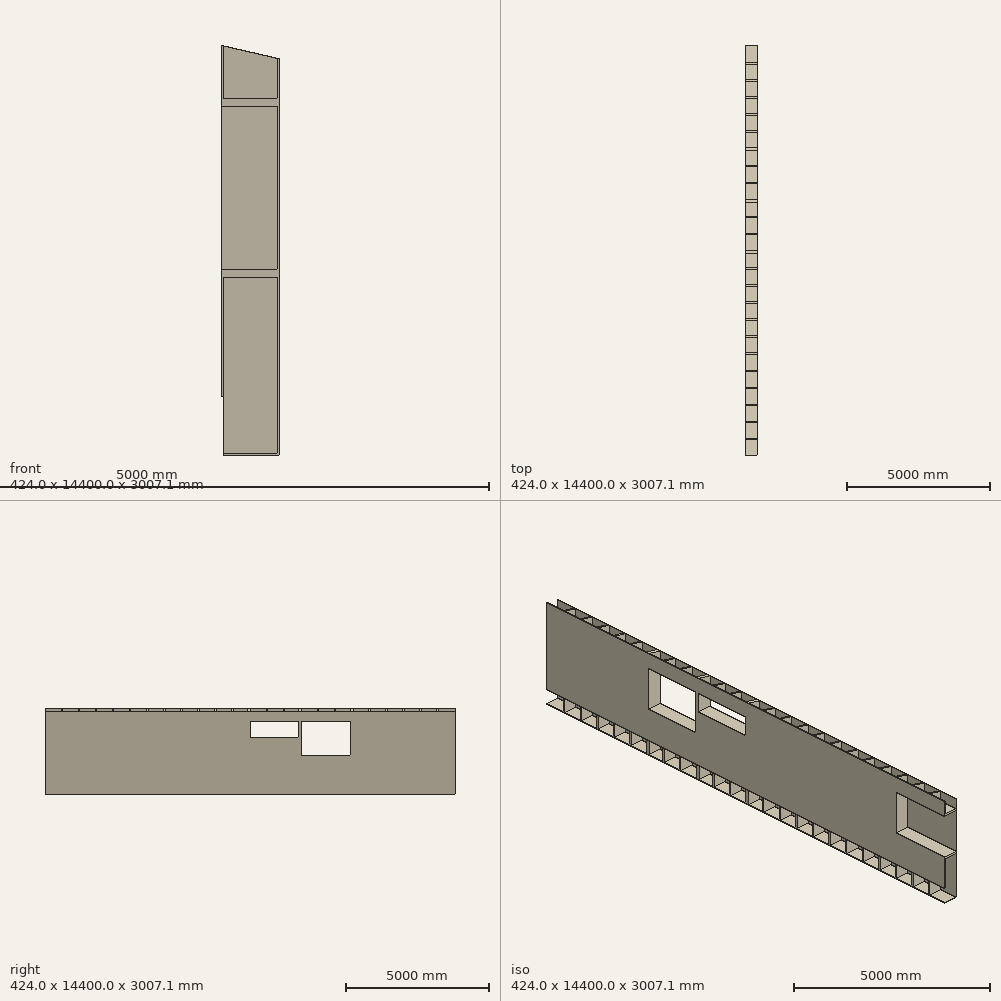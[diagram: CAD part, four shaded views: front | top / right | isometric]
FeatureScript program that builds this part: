
annotation { "Feature Type Name" : "Feature", "Feature Type Description" : "" }
export const myFeature = defineFeature(function(context is Context, id is Id, definition is map)
    precondition{}
    {
        {
            var Q0;
            Q0=qCreatedBy(makeId("Right.planeOp"),FACE);
            var sketch = newSketch(context, id + "F0", { "sketchPlane" : qUnion([Q0])});
            skLineSegment(sketch, "E0.bottom", {"start": v(0, 0) * mm, "end": v(14400, 0) * mm});
            skLineSegment(sketch, "E0.top", {"start": v(0, 3200) * mm, "end": v(14400, 3200) * mm});
            skLineSegment(sketch, "E0.left", {"start": v(0, 0) * mm, "end": v(0, 3200) * mm});
            skLineSegment(sketch, "E0.right", {"start": v(14400, 0) * mm, "end": v(14400, 3200) * mm});
            skLineSegment(sketch, "E1", {"start": v(549, 3200) * mm, "end": v(549, 2610) * mm});
            skLineSegment(sketch, "E2", {"start": v(600, 3200) * mm, "end": v(600, 2610) * mm});
            skLineSegment(sketch, "E3.1.0.0", {"start": v(1149, 3200) * mm, "end": v(1149, 2610) * mm});
            skLineSegment(sketch, "E3.1.0.1", {"start": v(1200, 3200) * mm, "end": v(1200, 2610) * mm});
            skLineSegment(sketch, "E3.2.0.0", {"start": v(1749, 3200) * mm, "end": v(1749, 0) * mm});
            skLineSegment(sketch, "E3.2.0.1", {"start": v(1800, 3200) * mm, "end": v(1800, 0) * mm});
            skLineSegment(sketch, "E3.3.0.0", {"start": v(2349, 3200) * mm, "end": v(2349, 0) * mm});
            skLineSegment(sketch, "E3.3.0.1", {"start": v(2400, 3200) * mm, "end": v(2400, 0) * mm});
            skLineSegment(sketch, "E3.4.0.0", {"start": v(2949, 3200) * mm, "end": v(2949, 0) * mm});
            skLineSegment(sketch, "E3.4.0.1", {"start": v(3000, 3200) * mm, "end": v(3000, 0) * mm});
            skLineSegment(sketch, "E3.5.0.0", {"start": v(3549, 3200) * mm, "end": v(3549, 0) * mm});
            skLineSegment(sketch, "E3.5.0.1", {"start": v(3600, 3200) * mm, "end": v(3600, 0) * mm});
            skLineSegment(sketch, "E3.6.0.0", {"start": v(4149, 3200) * mm, "end": v(4149, 0) * mm});
            skLineSegment(sketch, "E3.6.0.1", {"start": v(4200, 3200) * mm, "end": v(4200, 0) * mm});
            skLineSegment(sketch, "E3.7.0.0", {"start": v(4749, 3200) * mm, "end": v(4749, 0) * mm});
            skLineSegment(sketch, "E3.7.0.1", {"start": v(4800, 3200) * mm, "end": v(4800, 0) * mm});
            skLineSegment(sketch, "E3.8.0.0", {"start": v(5349, 3200) * mm, "end": v(5349, 0) * mm});
            skLineSegment(sketch, "E3.8.0.1", {"start": v(5400, 3200) * mm, "end": v(5400, 0) * mm});
            skLineSegment(sketch, "E3.9.0.0", {"start": v(5949, 3200) * mm, "end": v(5949, 0) * mm});
            skLineSegment(sketch, "E3.9.0.1", {"start": v(6000, 3200) * mm, "end": v(6000, 0) * mm});
            skLineSegment(sketch, "E3.10.0.0", {"start": v(6549, 3200) * mm, "end": v(6549, 0) * mm});
            skLineSegment(sketch, "E3.10.0.1", {"start": v(6600, 3200) * mm, "end": v(6600, 0) * mm});
            skLineSegment(sketch, "E3.11.0.1", {"start": v(7200, 3200) * mm, "end": v(7200, 2000) * mm});
            skLineSegment(sketch, "E3.12.0.0", {"start": v(7749, 3200) * mm, "end": v(7749, 2610) * mm});
            skLineSegment(sketch, "E3.12.0.1", {"start": v(7800, 3200) * mm, "end": v(7800, 2610) * mm});
            skLineSegment(sketch, "E3.13.0.0", {"start": v(8349, 3200) * mm, "end": v(8349, 2610) * mm});
            skLineSegment(sketch, "E3.13.0.1", {"start": v(8400, 3200) * mm, "end": v(8400, 2610) * mm});
            skLineSegment(sketch, "E3.14.0.1", {"start": v(9000, 3200) * mm, "end": v(9000, 2610) * mm});
            skLineSegment(sketch, "E3.15.0.0", {"start": v(9549, 3200) * mm, "end": v(9549, 2610) * mm});
            skLineSegment(sketch, "E3.15.0.1", {"start": v(9600, 3200) * mm, "end": v(9600, 2610) * mm});
            skLineSegment(sketch, "E3.16.0.0", {"start": v(10149, 3200) * mm, "end": v(10149, 2610) * mm});
            skLineSegment(sketch, "E3.16.0.1", {"start": v(10200, 3200) * mm, "end": v(10200, 2610) * mm});
            skLineSegment(sketch, "E3.17.0.0", {"start": v(10749, 3200) * mm, "end": v(10749, 0) * mm});
            skLineSegment(sketch, "E3.17.0.1", {"start": v(10800, 3200) * mm, "end": v(10800, 0) * mm});
            skLineSegment(sketch, "E3.18.0.0", {"start": v(11349, 3200) * mm, "end": v(11349, 0) * mm});
            skLineSegment(sketch, "E3.18.0.1", {"start": v(11400, 3200) * mm, "end": v(11400, 0) * mm});
            skLineSegment(sketch, "E3.19.0.0", {"start": v(11949, 3200) * mm, "end": v(11949, 0) * mm});
            skLineSegment(sketch, "E3.19.0.1", {"start": v(12000, 3200) * mm, "end": v(12000, 0) * mm});
            skLineSegment(sketch, "E3.20.0.0", {"start": v(12549, 3200) * mm, "end": v(12549, 0) * mm});
            skLineSegment(sketch, "E3.20.0.1", {"start": v(12600, 3200) * mm, "end": v(12600, 0) * mm});
            skLineSegment(sketch, "E3.21.0.0", {"start": v(13149, 3200) * mm, "end": v(13149, 0) * mm});
            skLineSegment(sketch, "E3.21.0.1", {"start": v(13200, 3200) * mm, "end": v(13200, 0) * mm});
            skLineSegment(sketch, "E3.22.0.0", {"start": v(13749, 3200) * mm, "end": v(13749, 0) * mm});
            skLineSegment(sketch, "E3.22.0.1", {"start": v(13800, 3200) * mm, "end": v(13800, 0) * mm});
            skLineSegment(sketch, "E3.direction1", {"start": v(549, 0) * mm, "end": v(1149, 0) * mm, "construction": true});
            skLineSegment(sketch, "E4", {"start": v(0, 2550) * mm, "end": v(1749, 2550) * mm});
            skLineSegment(sketch, "E5", {"start": v(0, 2610) * mm, "end": v(1749, 2610) * mm});
            skLineSegment(sketch, "E6", {"start": v(1740, 2550) * mm, "end": v(1740, 1350) * mm});
            skLineSegment(sketch, "E7", {"start": v(1749, 1350) * mm, "end": v(0, 1350) * mm});
            skLineSegment(sketch, "E8", {"start": v(1749, 1290) * mm, "end": v(0, 1290) * mm});
            skLineSegment(sketch, "E9.trimOffspring", {"start": v(549, 1290) * mm, "end": v(549, 0) * mm});
            skLineSegment(sketch, "E10.trimOffspring", {"start": v(600, 1290) * mm, "end": v(600, 0) * mm});
            skLineSegment(sketch, "E11.trimOffspring", {"start": v(1149, 1290) * mm, "end": v(1149, 0) * mm});
            skLineSegment(sketch, "E12.trimOffspring", {"start": v(1200, 1290) * mm, "end": v(1200, 0) * mm});
            skLineSegment(sketch, "E13", {"start": v(7200, 2610) * mm, "end": v(8898, 2610) * mm});
            skLineSegment(sketch, "E14", {"start": v(7200, 2550) * mm, "end": v(8898, 2550) * mm});
            skLineSegment(sketch, "E15", {"start": v(7200, 2000) * mm, "end": v(8898, 2000) * mm});
            skLineSegment(sketch, "E16", {"start": v(7200, 1940) * mm, "end": v(8898, 1940) * mm});
            skLineSegment(sketch, "E17.trimOffspring", {"start": v(7149, 3200) * mm, "end": v(7149, 0) * mm});
            skLineSegment(sketch, "E18.trimOffspring", {"start": v(7200, 1940) * mm, "end": v(7200, 0) * mm});
            skLineSegment(sketch, "E19.trimOffspring", {"start": v(7749, 1940) * mm, "end": v(7749, 0) * mm});
            skLineSegment(sketch, "E20.trimOffspring", {"start": v(7800, 1940) * mm, "end": v(7800, 0) * mm});
            skLineSegment(sketch, "E21", {"start": v(7098, 3200) * mm, "end": v(7098, 0) * mm});
            skLineSegment(sketch, "E22", {"start": v(9000, 3200) * mm, "end": v(9000, 0) * mm});
            skLineSegment(sketch, "E23", {"start": v(9000, 2610) * mm, "end": v(10698, 2610) * mm});
            skLineSegment(sketch, "E24", {"start": v(9000, 2550) * mm, "end": v(10698, 2550) * mm});
            skLineSegment(sketch, "E25", {"start": v(9000, 1350) * mm, "end": v(10698, 1350) * mm});
            skLineSegment(sketch, "E26", {"start": v(9000, 1290) * mm, "end": v(10698, 1290) * mm});
            skLineSegment(sketch, "E27.trimOffspring", {"start": v(8949, 3200) * mm, "end": v(8949, 0) * mm});
            skLineSegment(sketch, "E28.trimOffspring", {"start": v(9000, 1290) * mm, "end": v(9000, 0) * mm});
            skLineSegment(sketch, "E29.trimOffspring", {"start": v(9549, 1290) * mm, "end": v(9549, 0) * mm});
            skLineSegment(sketch, "E30.trimOffspring", {"start": v(9600, 1290) * mm, "end": v(9600, 0) * mm});
            skLineSegment(sketch, "E31.trimOffspring", {"start": v(10149, 1290) * mm, "end": v(10149, 0) * mm});
            skLineSegment(sketch, "E32.trimOffspring", {"start": v(8349, 1940) * mm, "end": v(8349, 0) * mm});
            skLineSegment(sketch, "E33.trimOffspring", {"start": v(8400, 1940) * mm, "end": v(8400, 0) * mm});
            skLineSegment(sketch, "E34", {"start": v(8898, 3200) * mm, "end": v(8898, 0) * mm});
            skLineSegment(sketch, "E35.trimOffspring", {"start": v(10200, 1290) * mm, "end": v(10200, 0) * mm});
            skLineSegment(sketch, "E36", {"start": v(10698, 3200) * mm, "end": v(10698, 0) * mm});
            skSolve(sketch);
        }
        {
            var Q0;
            {var subQ0=sQuery(id+"F0.wireOp",EDGE,"E1");Q0=makeQuery(id+"F0.imprint","IMPRINT",FACE,{"disambiguationData":[TD([[makeQuery(id+"F0.imprint","IMPRINT",EDGE,{"derivedFrom":subQ0}),1.0]])]});}
            var Q1;
            {var subQ0=sQuery(id+"F0.wireOp",EDGE,"E3.1.0.0");Q1=makeQuery(id+"F0.imprint","IMPRINT",FACE,{"disambiguationData":[TD([[makeQuery(id+"F0.imprint","IMPRINT",EDGE,{"derivedFrom":subQ0}),1.0]])]});}
            var Q2;
            {var subQ0=sQuery(id+"F0.wireOp",EDGE,"E3.2.0.0");Q2=makeQuery(id+"F0.imprint","IMPRINT",FACE,{"disambiguationData":[TD([[makeQuery(id+"F0.imprint","IMPRINT",EDGE,{"derivedFrom":subQ0}),1.0]])]});}
            var Q3;
            {var subQ0=sQuery(id+"F0.wireOp",EDGE,"E3.3.0.0");Q3=makeQuery(id+"F0.imprint","IMPRINT",FACE,{"disambiguationData":[TD([[makeQuery(id+"F0.imprint","IMPRINT",EDGE,{"derivedFrom":subQ0}),1.0]])]});}
            var Q4;
            {var subQ0=sQuery(id+"F0.wireOp",EDGE,"E3.4.0.0");Q4=makeQuery(id+"F0.imprint","IMPRINT",FACE,{"disambiguationData":[TD([[makeQuery(id+"F0.imprint","IMPRINT",EDGE,{"derivedFrom":subQ0}),1.0]])]});}
            var Q5;
            {var subQ0=sQuery(id+"F0.wireOp",EDGE,"E3.5.0.0");Q5=makeQuery(id+"F0.imprint","IMPRINT",FACE,{"disambiguationData":[TD([[makeQuery(id+"F0.imprint","IMPRINT",EDGE,{"derivedFrom":subQ0}),1.0]])]});}
            var Q6;
            {var subQ0=sQuery(id+"F0.wireOp",EDGE,"E3.6.0.0");Q6=makeQuery(id+"F0.imprint","IMPRINT",FACE,{"disambiguationData":[TD([[makeQuery(id+"F0.imprint","IMPRINT",EDGE,{"derivedFrom":subQ0}),1.0]])]});}
            var Q7;
            {var subQ0=sQuery(id+"F0.wireOp",EDGE,"E3.7.0.0");Q7=makeQuery(id+"F0.imprint","IMPRINT",FACE,{"disambiguationData":[TD([[makeQuery(id+"F0.imprint","IMPRINT",EDGE,{"derivedFrom":subQ0}),1.0]])]});}
            var Q8;
            {var subQ0=sQuery(id+"F0.wireOp",EDGE,"E3.8.0.0");Q8=makeQuery(id+"F0.imprint","IMPRINT",FACE,{"disambiguationData":[TD([[makeQuery(id+"F0.imprint","IMPRINT",EDGE,{"derivedFrom":subQ0}),1.0]])]});}
            var Q9;
            {var subQ0=sQuery(id+"F0.wireOp",EDGE,"E3.9.0.0");Q9=makeQuery(id+"F0.imprint","IMPRINT",FACE,{"disambiguationData":[TD([[makeQuery(id+"F0.imprint","IMPRINT",EDGE,{"derivedFrom":subQ0}),1.0]])]});}
            var Q10;
            {var subQ0=sQuery(id+"F0.wireOp",EDGE,"E3.10.0.0");Q10=makeQuery(id+"F0.imprint","IMPRINT",FACE,{"disambiguationData":[TD([[makeQuery(id+"F0.imprint","IMPRINT",EDGE,{"derivedFrom":subQ0}),1.0]])]});}
            var Q11;
            {var subQ0=sQuery(id+"F0.wireOp",EDGE,"E3.11.0.0");Q11=makeQuery(id+"F0.imprint","IMPRINT",FACE,{"disambiguationData":[TD([[makeQuery(id+"F0.imprint","IMPRINT",EDGE,{"derivedFrom":subQ0}),1.0]])]});}
            var Q12;
            {var subQ0=sQuery(id+"F0.wireOp",EDGE,"E3.12.0.0");Q12=makeQuery(id+"F0.imprint","IMPRINT",FACE,{"disambiguationData":[TD([[makeQuery(id+"F0.imprint","IMPRINT",EDGE,{"derivedFrom":subQ0}),1.0]])]});}
            var Q13;
            {var subQ0=sQuery(id+"F0.wireOp",EDGE,"E3.13.0.0");Q13=makeQuery(id+"F0.imprint","IMPRINT",FACE,{"disambiguationData":[TD([[makeQuery(id+"F0.imprint","IMPRINT",EDGE,{"derivedFrom":subQ0}),1.0]])]});}
            var Q14;
            {var subQ0=sQuery(id+"F0.wireOp",EDGE,"E3.14.0.0");Q14=makeQuery(id+"F0.imprint","IMPRINT",FACE,{"disambiguationData":[TD([[makeQuery(id+"F0.imprint","IMPRINT",EDGE,{"derivedFrom":subQ0}),1.0]])]});}
            var Q15;
            {var subQ0=sQuery(id+"F0.wireOp",EDGE,"E3.15.0.0");Q15=makeQuery(id+"F0.imprint","IMPRINT",FACE,{"disambiguationData":[TD([[makeQuery(id+"F0.imprint","IMPRINT",EDGE,{"derivedFrom":subQ0}),1.0]])]});}
            var Q16;
            {var subQ0=sQuery(id+"F0.wireOp",EDGE,"E3.16.0.0");Q16=makeQuery(id+"F0.imprint","IMPRINT",FACE,{"disambiguationData":[TD([[makeQuery(id+"F0.imprint","IMPRINT",EDGE,{"derivedFrom":subQ0}),1.0]])]});}
            var Q17;
            {var subQ0=sQuery(id+"F0.wireOp",EDGE,"E3.17.0.0");Q17=makeQuery(id+"F0.imprint","IMPRINT",FACE,{"disambiguationData":[TD([[makeQuery(id+"F0.imprint","IMPRINT",EDGE,{"derivedFrom":subQ0}),1.0]])]});}
            var Q18;
            {var subQ0=sQuery(id+"F0.wireOp",EDGE,"E3.18.0.0");Q18=makeQuery(id+"F0.imprint","IMPRINT",FACE,{"disambiguationData":[TD([[makeQuery(id+"F0.imprint","IMPRINT",EDGE,{"derivedFrom":subQ0}),1.0]])]});}
            var Q19;
            {var subQ0=sQuery(id+"F0.wireOp",EDGE,"E3.19.0.0");Q19=makeQuery(id+"F0.imprint","IMPRINT",FACE,{"disambiguationData":[TD([[makeQuery(id+"F0.imprint","IMPRINT",EDGE,{"derivedFrom":subQ0}),1.0]])]});}
            var Q20;
            {var subQ0=sQuery(id+"F0.wireOp",EDGE,"E3.20.0.0");Q20=makeQuery(id+"F0.imprint","IMPRINT",FACE,{"disambiguationData":[TD([[makeQuery(id+"F0.imprint","IMPRINT",EDGE,{"derivedFrom":subQ0}),1.0]])]});}
            var Q21;
            {var subQ0=sQuery(id+"F0.wireOp",EDGE,"E3.21.0.0");Q21=makeQuery(id+"F0.imprint","IMPRINT",FACE,{"disambiguationData":[TD([[makeQuery(id+"F0.imprint","IMPRINT",EDGE,{"derivedFrom":subQ0}),1.0]])]});}
            var Q22;
            {var subQ0=sQuery(id+"F0.wireOp",EDGE,"E3.22.0.0");Q22=makeQuery(id+"F0.imprint","IMPRINT",FACE,{"disambiguationData":[TD([[makeQuery(id+"F0.imprint","IMPRINT",EDGE,{"derivedFrom":subQ0}),1.0]])]});}
            var Q23;
            {var subQ0=sQuery(id+"F0.wireOp",EDGE,"E4");var subQ4=sQuery(id+"F0.wireOp",EDGE,"E0.left");var subQ5=makeQuery(id+"F0.imprint","INTERSECT",VERTEX,{"derivedFrom":[subQ4,subQ0]});Q23=makeQuery(id+"F0.imprint","IMPRINT",FACE,{"disambiguationData":[TD([[makeQuery(id+"F0.imprint","IMPRINT",EDGE,{"disambiguationData":[TD([[subQ5,-1.0]])],"derivedFrom":subQ4}),-1.0]])]});}
            var Q24;
            {var subQ0=sQuery(id+"F0.wireOp",EDGE,"E7");var subQ2=sQuery(id+"F0.wireOp",EDGE,"E0.left");var subQ3=makeQuery(id+"F0.imprint","INTERSECT",VERTEX,{"derivedFrom":[subQ2,subQ0]});Q24=makeQuery(id+"F0.imprint","IMPRINT",FACE,{"disambiguationData":[TD([[makeQuery(id+"F0.imprint","IMPRINT",EDGE,{"disambiguationData":[TD([[subQ3,1.0]])],"derivedFrom":subQ2}),-1.0]])]});}
            var Q25;
            {var subQ0=sQuery(id+"F0.wireOp",EDGE,"E11.trimOffspring");Q25=makeQuery(id+"F0.imprint","IMPRINT",FACE,{"disambiguationData":[TD([[makeQuery(id+"F0.imprint","IMPRINT",EDGE,{"derivedFrom":subQ0}),1.0]])]});}
            var Q26;
            {var subQ0=sQuery(id+"F0.wireOp",EDGE,"E9.trimOffspring");Q26=makeQuery(id+"F0.imprint","IMPRINT",FACE,{"disambiguationData":[TD([[makeQuery(id+"F0.imprint","IMPRINT",EDGE,{"derivedFrom":subQ0}),1.0]])]});}
            var Q27;
            {var subQ0=sQuery(id+"F0.wireOp",EDGE,"E17.trimOffspring");Q27=makeQuery(id+"F0.imprint","IMPRINT",FACE,{"disambiguationData":[TD([[makeQuery(id+"F0.imprint","IMPRINT",EDGE,{"derivedFrom":subQ0}),1.0]])]});}
            var Q28;
            {var subQ0=sQuery(id+"F0.wireOp",EDGE,"E19.trimOffspring");Q28=makeQuery(id+"F0.imprint","IMPRINT",FACE,{"disambiguationData":[TD([[makeQuery(id+"F0.imprint","IMPRINT",EDGE,{"derivedFrom":subQ0}),1.0]])]});}
            var Q29;
            {var subQ5=sQuery(id+"F0.wireOp",EDGE,"E24");Q29=makeQuery(id+"F0.imprint","IMPRINT",FACE,{"disambiguationData":[TD([[makeQuery(id+"F0.imprint","IMPRINT",EDGE,{"derivedFrom":subQ5}),1.0]])]});}
            var Q30;
            {var subQ0=sQuery(id+"F0.wireOp",EDGE,"E27.trimOffspring");Q30=makeQuery(id+"F0.imprint","IMPRINT",FACE,{"disambiguationData":[TD([[makeQuery(id+"F0.imprint","IMPRINT",EDGE,{"derivedFrom":subQ0}),1.0]])]});}
            var Q31;
            {var subQ0=sQuery(id+"F0.wireOp",EDGE,"E29.trimOffspring");Q31=makeQuery(id+"F0.imprint","IMPRINT",FACE,{"disambiguationData":[TD([[makeQuery(id+"F0.imprint","IMPRINT",EDGE,{"derivedFrom":subQ0}),1.0]])]});}
            var Q32;
            {var subQ0=sQuery(id+"F0.wireOp",EDGE,"E17.trimOffspring");Q32=makeQuery(id+"F0.imprint","IMPRINT",FACE,{"disambiguationData":[TD([[makeQuery(id+"F0.imprint","IMPRINT",EDGE,{"derivedFrom":subQ0}),-1.0]])]});}
            var Q33;
            {var subQ6=sQuery(id+"F0.wireOp",EDGE,"E14");Q33=makeQuery(id+"F0.imprint","IMPRINT",FACE,{"disambiguationData":[TD([[makeQuery(id+"F0.imprint","IMPRINT",EDGE,{"derivedFrom":subQ6}),1.0]])]});}
            var Q34;
            {var subQ5=sQuery(id+"F0.wireOp",EDGE,"E25");Q34=makeQuery(id+"F0.imprint","IMPRINT",FACE,{"disambiguationData":[TD([[makeQuery(id+"F0.imprint","IMPRINT",EDGE,{"derivedFrom":subQ5}),-1.0]])]});}
            var Q35;
            {var subQ4=sQuery(id+"F0.wireOp",EDGE,"E27.trimOffspring");Q35=makeQuery(id+"F0.imprint","IMPRINT",FACE,{"disambiguationData":[TD([[makeQuery(id+"F0.imprint","IMPRINT",EDGE,{"derivedFrom":subQ4}),-1.0]])]});}
            var Q36;
            {var subQ0=sQuery(id+"F0.wireOp",EDGE,"E31.trimOffspring");Q36=makeQuery(id+"F0.imprint","IMPRINT",FACE,{"disambiguationData":[TD([[makeQuery(id+"F0.imprint","IMPRINT",EDGE,{"derivedFrom":subQ0}),1.0]])]});}
            var Q37;
            {var subQ4=sQuery(id+"F0.wireOp",EDGE,"E3.17.0.0");Q37=makeQuery(id+"F0.imprint","IMPRINT",FACE,{"disambiguationData":[TD([[makeQuery(id+"F0.imprint","IMPRINT",EDGE,{"derivedFrom":subQ4}),-1.0]])]});}
            var Q38;
            {var subQ0=sQuery(id+"F0.wireOp",EDGE,"E32.trimOffspring");Q38=makeQuery(id+"F0.imprint","IMPRINT",FACE,{"disambiguationData":[TD([[makeQuery(id+"F0.imprint","IMPRINT",EDGE,{"derivedFrom":subQ0}),1.0]])]});}
            extrude(context, id + "F1", {"entities" : qUnion([Q0, Q1, Q2, Q3, Q4, Q5, Q6, Q7, Q8, Q9, Q10, Q11, Q12, Q13, Q14, Q15, Q16, Q17, Q18, Q19, Q20, Q21, Q22, Q23, Q24, Q25, Q26, Q27, Q28, Q29, Q30, Q31, Q32, Q33, Q34, Q35, Q36, Q37, Q38]), "depth" : 400 * mm, "offsetDistance" : 25 * mm});
        }
        {
            var Q0;
            Q0=makeQuery(id+"F1.opExtrude","CAP_FACE",FACE,{"disambiguationData":[OSD([sQuery(id+"F0.wireOp",EDGE,"E0.bottom"),sQuery(id+"F0.wireOp",EDGE,"E0.top"),sQuery(id+"F0.wireOp",EDGE,"E1"),sQuery(id+"F0.wireOp",EDGE,"E2")])],"isStart":false});
            var sketch = newSketch(context, id + "F2", { "sketchPlane" : qUnion([Q0])});
            skLineSegment(sketch, "E37.bottom", {"start": v(0, 3200) * mm, "end": v(14400, 3200) * mm});
            skLineSegment(sketch, "E37.top", {"start": v(0, 0) * mm, "end": v(14400, 0) * mm});
            skLineSegment(sketch, "E37.left", {"start": v(0, 3200) * mm, "end": v(0, 0) * mm});
            skLineSegment(sketch, "E37.right", {"start": v(14400, 3200) * mm, "end": v(14400, 0) * mm});
            skLineSegment(sketch, "E38.bottom", {"start": v(0, 2550) * mm, "end": v(1749, 2550) * mm});
            skLineSegment(sketch, "E38.top", {"start": v(0, 1350) * mm, "end": v(1749, 1350) * mm});
            skLineSegment(sketch, "E38.left", {"start": v(0, 2550) * mm, "end": v(0, 1350) * mm});
            skLineSegment(sketch, "E38.right", {"start": v(1749, 2550) * mm, "end": v(1749, 1350) * mm});
            skLineSegment(sketch, "E39.bottom", {"start": v(7200, 2550) * mm, "end": v(8898, 2550) * mm});
            skLineSegment(sketch, "E39.top", {"start": v(7200, 2000) * mm, "end": v(8898, 2000) * mm});
            skLineSegment(sketch, "E39.left", {"start": v(7200, 2000) * mm, "end": v(7200, 2550) * mm});
            skLineSegment(sketch, "E39.right", {"start": v(8898, 2550) * mm, "end": v(8898, 2000) * mm});
            skLineSegment(sketch, "E40.bottom", {"start": v(9000, 2550) * mm, "end": v(10698, 2550) * mm});
            skLineSegment(sketch, "E40.top", {"start": v(9000, 1350) * mm, "end": v(10698, 1350) * mm});
            skLineSegment(sketch, "E40.left", {"start": v(9000, 2550) * mm, "end": v(9000, 1350) * mm});
            skLineSegment(sketch, "E40.right", {"start": v(10698, 2550) * mm, "end": v(10698, 1350) * mm});
            skSolve(sketch);
        }
        {
            var Q0;
            {var subQ0=sQuery(id+"F0.wireOp",EDGE,"IgmUadhF-glSP-F6cX-IuOI-NBYm0LEYq7ye.right");Q0=makeQuery(id+"F2.imprint","IMPRINT",FACE,{"disambiguationData":[TD([[makeQuery(id+"F2.imprint","IMPRINT",EDGE,{"derivedFrom":makeQuery(id+"FR5aaBEQjmpf4qQ_0.opExtrude","CAP_EDGE",EDGE,{"disambiguationData":[OSD([subQ0])],"isStart":false})}),1.0]])]});}
            var Q1;
            {var subQ0=sQuery(id+"F0.wireOp",EDGE,"e199f144-8a5d-4ce1-bf45-a125ad6e8049.1.0.1");Q1=makeQuery(id+"F2.imprint","IMPRINT",FACE,{"disambiguationData":[TD([[makeQuery(id+"F2.imprint","IMPRINT",EDGE,{"derivedFrom":makeQuery(id+"FR5aaBEQjmpf4qQ_0.opExtrude","CAP_EDGE",EDGE,{"disambiguationData":[OSD([subQ0])],"isStart":false})}),1.0]])]});}
            var Q2;
            {var subQ0=sQuery(id+"F0.wireOp",EDGE,"7G1fydb4-uLTL-noCV-z4Kh-rXlVpRovcI43.top");var subQ1=sQuery(id+"F0.wireOp",EDGE,"e199f144-8a5d-4ce1-bf45-a125ad6e8049.2.0.1");var subQ2=makeQuery(id+"F0.imprint","INTERSECT",VERTEX,{"derivedFrom":[subQ1,subQ0]});Q2=makeQuery(id+"F2.imprint","IMPRINT",FACE,{"disambiguationData":[TD([[makeQuery(id+"F2.imprint","IMPRINT",EDGE,{"derivedFrom":makeQuery(id+"FR5aaBEQjmpf4qQ_0.opExtrude","CAP_EDGE",EDGE,{"disambiguationData":[OSD([subQ1]),TDD([makeQuery(id+"F0.imprint","IMPRINT",EDGE,{"disambiguationData":[TD([[subQ2,-1.0]])],"derivedFrom":subQ1})])],"isStart":false})}),1.0]])]});}
            var Q3;
            {var subQ0=sQuery(id+"F0.wireOp",EDGE,"UVeaEfiz-wVvE-Ytuf-kFiL-HFISCNqZgDvp");var subQ1=sQuery(id+"F0.wireOp",EDGE,"e199f144-8a5d-4ce1-bf45-a125ad6e8049.2.0.1");var subQ2=makeQuery(id+"F0.imprint","INTERSECT",VERTEX,{"derivedFrom":[subQ1,subQ0]});Q3=makeQuery(id+"F2.imprint","IMPRINT",FACE,{"disambiguationData":[TD([[makeQuery(id+"F2.imprint","IMPRINT",EDGE,{"derivedFrom":makeQuery(id+"FR5aaBEQjmpf4qQ_0.opExtrude","CAP_EDGE",EDGE,{"disambiguationData":[OSD([subQ1]),TDD([makeQuery(id+"F0.imprint","IMPRINT",EDGE,{"disambiguationData":[TD([[subQ2,-1.0]])],"derivedFrom":subQ1})])],"isStart":false})}),1.0]])]});}
            var Q4;
            {var subQ0=sQuery(id+"F0.wireOp",EDGE,"7G1fydb4-uLTL-noCV-z4Kh-rXlVpRovcI43.top");var subQ1=sQuery(id+"F0.wireOp",EDGE,"e199f144-8a5d-4ce1-bf45-a125ad6e8049.3.0.1");var subQ2=makeQuery(id+"F0.imprint","INTERSECT",VERTEX,{"derivedFrom":[subQ1,subQ0]});Q4=makeQuery(id+"F2.imprint","IMPRINT",FACE,{"disambiguationData":[TD([[makeQuery(id+"F2.imprint","IMPRINT",EDGE,{"derivedFrom":makeQuery(id+"FR5aaBEQjmpf4qQ_0.opExtrude","CAP_EDGE",EDGE,{"disambiguationData":[OSD([subQ1]),TDD([makeQuery(id+"F0.imprint","IMPRINT",EDGE,{"disambiguationData":[TD([[subQ2,-1.0]])],"derivedFrom":subQ1})])],"isStart":false})}),1.0]])]});}
            var Q5;
            {var subQ0=sQuery(id+"F0.wireOp",EDGE,"UVeaEfiz-wVvE-Ytuf-kFiL-HFISCNqZgDvp");var subQ1=sQuery(id+"F0.wireOp",EDGE,"e199f144-8a5d-4ce1-bf45-a125ad6e8049.3.0.1");var subQ2=makeQuery(id+"F0.imprint","INTERSECT",VERTEX,{"derivedFrom":[subQ1,subQ0]});Q5=makeQuery(id+"F2.imprint","IMPRINT",FACE,{"disambiguationData":[TD([[makeQuery(id+"F2.imprint","IMPRINT",EDGE,{"derivedFrom":makeQuery(id+"FR5aaBEQjmpf4qQ_0.opExtrude","CAP_EDGE",EDGE,{"disambiguationData":[OSD([subQ1]),TDD([makeQuery(id+"F0.imprint","IMPRINT",EDGE,{"disambiguationData":[TD([[subQ2,-1.0]])],"derivedFrom":subQ1})])],"isStart":false})}),1.0]])]});}
            var Q6;
            {var subQ3=sQuery(id+"F0.wireOp",EDGE,"6a5vYrMW-g177-bs2h-nKDJ-oBlYrjlF6iIu.bottom");Q6=makeQuery(id+"F2.imprint","IMPRINT",FACE,{"disambiguationData":[TD([[makeQuery(id+"F2.imprint","IMPRINT",EDGE,{"derivedFrom":makeQuery(id+"FR5aaBEQjmpf4qQ_0.opExtrude","CAP_EDGE",EDGE,{"disambiguationData":[OSD([subQ3])],"isStart":false})}),1.0]])]});}
            var Q7;
            {var subQ0=sQuery(id+"F0.wireOp",EDGE,"gnOSFfbY-vuvK-LYlP-5ctm-sZ0Oh0ULgJPw.bottom");Q7=makeQuery(id+"F2.imprint","IMPRINT",FACE,{"disambiguationData":[TD([[makeQuery(id+"F2.imprint","IMPRINT",EDGE,{"derivedFrom":makeQuery(id+"FR5aaBEQjmpf4qQ_0.opExtrude","CAP_EDGE",EDGE,{"disambiguationData":[OSD([subQ0])],"isStart":false})}),1.0]])]});}
            var Q8;
            {var subQ0=sQuery(id+"F0.wireOp",EDGE,"e199f144-8a5d-4ce1-bf45-a125ad6e8049.5.0.1");Q8=makeQuery(id+"F2.imprint","IMPRINT",FACE,{"disambiguationData":[TD([[makeQuery(id+"F2.imprint","IMPRINT",EDGE,{"derivedFrom":makeQuery(id+"FR5aaBEQjmpf4qQ_0.opExtrude","CAP_EDGE",EDGE,{"disambiguationData":[OSD([subQ0])],"isStart":false})}),1.0]])]});}
            var Q9;
            {var subQ0=sQuery(id+"F0.wireOp",EDGE,"e199f144-8a5d-4ce1-bf45-a125ad6e8049.6.0.1");Q9=makeQuery(id+"F2.imprint","IMPRINT",FACE,{"disambiguationData":[TD([[makeQuery(id+"F2.imprint","IMPRINT",EDGE,{"derivedFrom":makeQuery(id+"FR5aaBEQjmpf4qQ_0.opExtrude","CAP_EDGE",EDGE,{"disambiguationData":[OSD([subQ0])],"isStart":false})}),1.0]])]});}
            var Q10;
            {var subQ0=sQuery(id+"F0.wireOp",EDGE,"7G1fydb4-uLTL-noCV-z4Kh-rXlVpRovcI43.top");var subQ1=sQuery(id+"F0.wireOp",EDGE,"e199f144-8a5d-4ce1-bf45-a125ad6e8049.8.0.0");var subQ2=makeQuery(id+"F0.imprint","INTERSECT",VERTEX,{"derivedFrom":[subQ1,subQ0]});Q10=makeQuery(id+"F2.imprint","IMPRINT",FACE,{"disambiguationData":[TD([[makeQuery(id+"F2.imprint","IMPRINT",EDGE,{"derivedFrom":makeQuery(id+"FR5aaBEQjmpf4qQ_0.opExtrude","CAP_EDGE",EDGE,{"disambiguationData":[OSD([subQ1]),TDD([makeQuery(id+"F0.imprint","IMPRINT",EDGE,{"disambiguationData":[TD([[subQ2,-1.0]])],"derivedFrom":subQ1})])],"isStart":false})}),-1.0]])]});}
            var Q11;
            {var subQ0=sQuery(id+"F0.wireOp",EDGE,"7Pknb1pR-AQNL-vs4c-cftO-efw3qLqmWL3U.top");var subQ1=sQuery(id+"F0.wireOp",EDGE,"e199f144-8a5d-4ce1-bf45-a125ad6e8049.8.0.0");var subQ2=makeQuery(id+"F0.imprint","INTERSECT",VERTEX,{"derivedFrom":[subQ1,subQ0]});Q11=makeQuery(id+"F2.imprint","IMPRINT",FACE,{"disambiguationData":[TD([[makeQuery(id+"F2.imprint","IMPRINT",EDGE,{"derivedFrom":makeQuery(id+"FR5aaBEQjmpf4qQ_0.opExtrude","CAP_EDGE",EDGE,{"disambiguationData":[OSD([subQ1]),TDD([makeQuery(id+"F0.imprint","IMPRINT",EDGE,{"disambiguationData":[TD([[subQ2,-1.0]])],"derivedFrom":subQ1})])],"isStart":false})}),-1.0]])]});}
            var Q12;
            {var subQ0=sQuery(id+"F0.wireOp",EDGE,"7G1fydb4-uLTL-noCV-z4Kh-rXlVpRovcI43.top");var subQ1=sQuery(id+"F0.wireOp",EDGE,"e199f144-8a5d-4ce1-bf45-a125ad6e8049.9.0.0");var subQ2=makeQuery(id+"F0.imprint","INTERSECT",VERTEX,{"derivedFrom":[subQ1,subQ0]});Q12=makeQuery(id+"F2.imprint","IMPRINT",FACE,{"disambiguationData":[TD([[makeQuery(id+"F2.imprint","IMPRINT",EDGE,{"derivedFrom":makeQuery(id+"FR5aaBEQjmpf4qQ_0.opExtrude","CAP_EDGE",EDGE,{"disambiguationData":[OSD([subQ1]),TDD([makeQuery(id+"F0.imprint","IMPRINT",EDGE,{"disambiguationData":[TD([[subQ2,-1.0]])],"derivedFrom":subQ1})])],"isStart":false})}),-1.0]])]});}
            var Q13;
            {var subQ3=sQuery(id+"F0.wireOp",EDGE,"gXg7DxGN-gq9m-dGJN-wiVj-4l8huUNlM5jk.top");var subQ4=sQuery(id+"F0.wireOp",EDGE,"PS9W6Kxl-IFaW-gl0p-Raxb-pY61IYD0TAJN.top");Q13=makeQuery(id+"F2.imprint","IMPRINT",FACE,{"disambiguationData":[TD([[makeQuery(id+"F2.imprint","IMPRINT",EDGE,{"derivedFrom":makeQuery(id+"FR5aaBEQjmpf4qQ_0.opExtrude","CAP_EDGE",EDGE,{"disambiguationData":[OSD([subQ3,subQ4])],"isStart":false})}),1.0]])]});}
            var Q14;
            {var subQ0=sQuery(id+"F0.wireOp",EDGE,"7G1fydb4-uLTL-noCV-z4Kh-rXlVpRovcI43.top");var subQ1=sQuery(id+"F0.wireOp",EDGE,"e199f144-8a5d-4ce1-bf45-a125ad6e8049.11.0.0");var subQ2=makeQuery(id+"F0.imprint","INTERSECT",VERTEX,{"derivedFrom":[subQ1,subQ0]});Q14=makeQuery(id+"F2.imprint","IMPRINT",FACE,{"disambiguationData":[TD([[makeQuery(id+"F2.imprint","IMPRINT",EDGE,{"derivedFrom":makeQuery(id+"FR5aaBEQjmpf4qQ_0.opExtrude","CAP_EDGE",EDGE,{"disambiguationData":[OSD([subQ1]),TDD([makeQuery(id+"F0.imprint","IMPRINT",EDGE,{"disambiguationData":[TD([[subQ2,-1.0]])],"derivedFrom":subQ1})])],"isStart":false})}),-1.0]])]});}
            var Q15;
            {var subQ0=sQuery(id+"F0.wireOp",EDGE,"7Pknb1pR-AQNL-vs4c-cftO-efw3qLqmWL3U.top");var subQ1=sQuery(id+"F0.wireOp",EDGE,"e199f144-8a5d-4ce1-bf45-a125ad6e8049.11.0.0");var subQ2=makeQuery(id+"F0.imprint","INTERSECT",VERTEX,{"derivedFrom":[subQ1,subQ0]});Q15=makeQuery(id+"F2.imprint","IMPRINT",FACE,{"disambiguationData":[TD([[makeQuery(id+"F2.imprint","IMPRINT",EDGE,{"derivedFrom":makeQuery(id+"FR5aaBEQjmpf4qQ_0.opExtrude","CAP_EDGE",EDGE,{"disambiguationData":[OSD([subQ1]),TDD([makeQuery(id+"F0.imprint","IMPRINT",EDGE,{"disambiguationData":[TD([[subQ2,-1.0]])],"derivedFrom":subQ1})])],"isStart":false})}),-1.0]])]});}
            var Q16;
            {var subQ0=sQuery(id+"F0.wireOp",EDGE,"e199f144-8a5d-4ce1-bf45-a125ad6e8049.12.0.0");Q16=makeQuery(id+"F2.imprint","IMPRINT",FACE,{"disambiguationData":[TD([[makeQuery(id+"F2.imprint","IMPRINT",EDGE,{"derivedFrom":makeQuery(id+"FR5aaBEQjmpf4qQ_0.opExtrude","CAP_EDGE",EDGE,{"disambiguationData":[OSD([subQ0])],"isStart":false})}),-1.0]])]});}
            var Q17;
            {var subQ0=sQuery(id+"F0.wireOp",EDGE,"e199f144-8a5d-4ce1-bf45-a125ad6e8049.12.0.1");Q17=makeQuery(id+"F2.imprint","IMPRINT",FACE,{"disambiguationData":[TD([[makeQuery(id+"F2.imprint","IMPRINT",EDGE,{"derivedFrom":makeQuery(id+"FR5aaBEQjmpf4qQ_0.opExtrude","CAP_EDGE",EDGE,{"disambiguationData":[OSD([subQ0])],"isStart":false})}),1.0]])]});}
            var Q18;
            {var subQ0=sQuery(id+"F0.wireOp",EDGE,"e199f144-8a5d-4ce1-bf45-a125ad6e8049.13.0.1");Q18=makeQuery(id+"F2.imprint","IMPRINT",FACE,{"disambiguationData":[TD([[makeQuery(id+"F2.imprint","IMPRINT",EDGE,{"derivedFrom":makeQuery(id+"FR5aaBEQjmpf4qQ_0.opExtrude","CAP_EDGE",EDGE,{"disambiguationData":[OSD([subQ0])],"isStart":false})}),1.0]])]});}
            var Q19;
            {var subQ0=sQuery(id+"F0.wireOp",EDGE,"e199f144-8a5d-4ce1-bf45-a125ad6e8049.14.0.1");Q19=makeQuery(id+"F2.imprint","IMPRINT",FACE,{"disambiguationData":[TD([[makeQuery(id+"F2.imprint","IMPRINT",EDGE,{"derivedFrom":makeQuery(id+"FR5aaBEQjmpf4qQ_0.opExtrude","CAP_EDGE",EDGE,{"disambiguationData":[OSD([subQ0])],"isStart":false})}),1.0]])]});}
            var Q20;
            {var subQ0=sQuery(id+"F0.wireOp",EDGE,"e199f144-8a5d-4ce1-bf45-a125ad6e8049.15.0.1");Q20=makeQuery(id+"F2.imprint","IMPRINT",FACE,{"disambiguationData":[TD([[makeQuery(id+"F2.imprint","IMPRINT",EDGE,{"derivedFrom":makeQuery(id+"FR5aaBEQjmpf4qQ_0.opExtrude","CAP_EDGE",EDGE,{"disambiguationData":[OSD([subQ0])],"isStart":false})}),1.0]])]});}
            var Q21;
            {var subQ0=sQuery(id+"F0.wireOp",EDGE,"e199f144-8a5d-4ce1-bf45-a125ad6e8049.16.0.1");Q21=makeQuery(id+"F2.imprint","IMPRINT",FACE,{"disambiguationData":[TD([[makeQuery(id+"F2.imprint","IMPRINT",EDGE,{"derivedFrom":makeQuery(id+"FR5aaBEQjmpf4qQ_0.opExtrude","CAP_EDGE",EDGE,{"disambiguationData":[OSD([subQ0])],"isStart":false})}),1.0]])]});}
            var Q22;
            {var subQ0=sQuery(id+"F0.wireOp",EDGE,"e199f144-8a5d-4ce1-bf45-a125ad6e8049.17.0.1");Q22=makeQuery(id+"F2.imprint","IMPRINT",FACE,{"disambiguationData":[TD([[makeQuery(id+"F2.imprint","IMPRINT",EDGE,{"derivedFrom":makeQuery(id+"FR5aaBEQjmpf4qQ_0.opExtrude","CAP_EDGE",EDGE,{"disambiguationData":[OSD([subQ0])],"isStart":false})}),1.0]])]});}
            var Q23;
            {var subQ0=sQuery(id+"F0.wireOp",EDGE,"bRGHuE3Z-0UxG-XqGQ-UJvl-NodW1FxR47Sy.right");var subQ5=sQuery(id+"F0.wireOp",EDGE,"7Pknb1pR-AQNL-vs4c-cftO-efw3qLqmWL3U.top");var subQ6=makeQuery(id+"F0.imprint","INTERSECT",VERTEX,{"derivedFrom":[subQ0,subQ5]});Q23=makeQuery(id+"F2.imprint","IMPRINT",FACE,{"disambiguationData":[TD([[makeQuery(id+"F2.imprint","IMPRINT",EDGE,{"derivedFrom":makeQuery(id+"FR5aaBEQjmpf4qQ_0.opExtrude","CAP_EDGE",EDGE,{"disambiguationData":[OSD([subQ5]),TDD([makeQuery(id+"F0.imprint","IMPRINT",EDGE,{"disambiguationData":[TD([[subQ6,-1.0]])],"derivedFrom":subQ5})])],"isStart":false})}),1.0]])]});}
            var Q24;
            {var subQ0=sQuery(id+"F0.wireOp",EDGE,"4a16b1b5-454c-480c-b834-8eaf71152ecc.3.18.0");Q24=makeQuery(id+"F2.imprint","IMPRINT",FACE,{"disambiguationData":[TD([[makeQuery(id+"F2.imprint","IMPRINT",EDGE,{"derivedFrom":makeQuery(id+"FR5aaBEQjmpf4qQ_0.opExtrude","CAP_EDGE",EDGE,{"disambiguationData":[OSD([subQ0])],"isStart":false})}),1.0]])]});}
            var Q25;
            {var subQ0=sQuery(id+"F0.wireOp",EDGE,"4a16b1b5-454c-480c-b834-8eaf71152ecc.3.19.0");Q25=makeQuery(id+"F2.imprint","IMPRINT",FACE,{"disambiguationData":[TD([[makeQuery(id+"F2.imprint","IMPRINT",EDGE,{"derivedFrom":makeQuery(id+"FR5aaBEQjmpf4qQ_0.opExtrude","CAP_EDGE",EDGE,{"disambiguationData":[OSD([subQ0])],"isStart":false})}),1.0]])]});}
            var Q26;
            {var subQ0=sQuery(id+"F0.wireOp",EDGE,"595e7557-905a-4d6e-8d03-79912b34425f.3.20.0");Q26=makeQuery(id+"F2.imprint","IMPRINT",FACE,{"disambiguationData":[TD([[makeQuery(id+"F2.imprint","IMPRINT",EDGE,{"derivedFrom":makeQuery(id+"FR5aaBEQjmpf4qQ_0.opExtrude","CAP_EDGE",EDGE,{"disambiguationData":[OSD([subQ0])],"isStart":false})}),1.0]])]});}
            var Q27;
            {var subQ0=sQuery(id+"F0.wireOp",EDGE,"f23ba9a7-b1a7-4011-84b8-e3fe6da358bf.3.21.0");Q27=makeQuery(id+"F2.imprint","IMPRINT",FACE,{"disambiguationData":[TD([[makeQuery(id+"F2.imprint","IMPRINT",EDGE,{"derivedFrom":makeQuery(id+"FR5aaBEQjmpf4qQ_0.opExtrude","CAP_EDGE",EDGE,{"disambiguationData":[OSD([subQ0])],"isStart":false})}),1.0]])]});}
            var Q28;
            {var subQ0=sQuery(id+"F0.wireOp",EDGE,"2q1XqnOg-X2X1-n0p0-nEM1-kVDvpq9L0III.right");Q28=makeQuery(id+"F2.imprint","IMPRINT",FACE,{"disambiguationData":[TD([[makeQuery(id+"F2.imprint","IMPRINT",EDGE,{"derivedFrom":makeQuery(id+"FR5aaBEQjmpf4qQ_0.opExtrude","CAP_EDGE",EDGE,{"disambiguationData":[OSD([subQ0])],"isStart":false})}),-1.0]])]});}
            var Q29;
            {var subQ1=sQuery(id+"F0.wireOp",EDGE,"7G1fydb4-uLTL-noCV-z4Kh-rXlVpRovcI43.top");var subQ3=sQuery(id+"F0.wireOp",EDGE,"6TiXDfr5-4Zk0-5UiI-dzMr-kruXfkv2xe0F.right");var subQ4=makeQuery(id+"F0.imprint","INTERSECT",VERTEX,{"derivedFrom":[subQ1,subQ3]});Q29=makeQuery(id+"F2.imprint","IMPRINT",FACE,{"disambiguationData":[TD([[makeQuery(id+"F2.imprint","IMPRINT",EDGE,{"derivedFrom":makeQuery(id+"FR5aaBEQjmpf4qQ_0.opExtrude","CAP_EDGE",EDGE,{"disambiguationData":[OSD([subQ3]),TDD([makeQuery(id+"F0.imprint","IMPRINT",EDGE,{"disambiguationData":[TD([[subQ4,-1.0]])],"derivedFrom":subQ3})])],"isStart":false})}),1.0]])]});}
            var Q30;
            {var subQ88=sQuery(id+"F2.wireOp",EDGE,"E37.right");Q30=makeQuery(id+"F2.imprint","IMPRINT",FACE,{"disambiguationData":[TD([[makeQuery(id+"F2.imprint","IMPRINT",EDGE,{"derivedFrom":subQ88}),-1.0]])]});}
            var Q31;
            {var subQ2=sQuery(id+"F2.wireOp",EDGE,"E37.left");Q31=makeQuery(id+"F2.imprint","IMPRINT",FACE,{"disambiguationData":[TD([[makeQuery(id+"F2.imprint","IMPRINT",EDGE,{"derivedFrom":subQ2}),1.0]])]});}
            var Q32;
            {var subQ1=makeQuery(id+"F1.opExtrude","CAP_EDGE",EDGE,{"disambiguationData":[OSD([sQuery(id+"F0.wireOp",EDGE,"E1")])],"isStart":false});Q32=makeQuery(id+"F2.imprint","IMPRINT",FACE,{"disambiguationData":[TD([[makeQuery(id+"F2.imprint","IMPRINT",EDGE,{"derivedFrom":subQ1}),1.0]])]});}
            var Q33;
            {var subQ1=sQuery(id+"F0.wireOp",EDGE,"E2");var subQ2=makeQuery(id+"F1.opExtrude","CAP_EDGE",EDGE,{"disambiguationData":[OSD([subQ1])],"isStart":false});Q33=makeQuery(id+"F2.imprint","IMPRINT",FACE,{"disambiguationData":[TD([[makeQuery(id+"F2.imprint","IMPRINT",EDGE,{"derivedFrom":subQ2}),1.0]])]});}
            var Q34;
            {var subQ1=sQuery(id+"F0.wireOp",EDGE,"E3.1.0.1");var subQ2=makeQuery(id+"F1.opExtrude","CAP_EDGE",EDGE,{"disambiguationData":[OSD([subQ1])],"isStart":false});Q34=makeQuery(id+"F2.imprint","IMPRINT",FACE,{"disambiguationData":[TD([[makeQuery(id+"F2.imprint","IMPRINT",EDGE,{"derivedFrom":subQ2}),1.0]])]});}
            var Q35;
            {var subQ5=sQuery(id+"F0.wireOp",EDGE,"E12.trimOffspring");var subQ6=makeQuery(id+"F1.opExtrude","CAP_EDGE",EDGE,{"disambiguationData":[OSD([subQ5])],"isStart":false});Q35=makeQuery(id+"F2.imprint","IMPRINT",FACE,{"disambiguationData":[TD([[makeQuery(id+"F2.imprint","IMPRINT",EDGE,{"derivedFrom":subQ6}),1.0]])]});}
            var Q36;
            {var subQ1=sQuery(id+"F0.wireOp",EDGE,"E10.trimOffspring");var subQ2=makeQuery(id+"F1.opExtrude","CAP_EDGE",EDGE,{"disambiguationData":[OSD([subQ1])],"isStart":false});Q36=makeQuery(id+"F2.imprint","IMPRINT",FACE,{"disambiguationData":[TD([[makeQuery(id+"F2.imprint","IMPRINT",EDGE,{"derivedFrom":subQ2}),1.0]])]});}
            extrude(context, id + "F3", {"entities" : qUnion([Q0, Q1, Q2, Q3, Q4, Q5, Q6, Q7, Q8, Q9, Q10, Q11, Q12, Q13, Q14, Q15, Q16, Q17, Q18, Q19, Q20, Q21, Q22, Q23, Q24, Q25, Q26, Q27, Q28, Q29, Q30, Q31, Q32, Q33, Q34, Q35, Q36]), "operationType" : NewBodyOperationType.ADD, "depth" : 12 * mm, "offsetDistance" : 25 * mm});
        }
        {
            var Q0;
            Q0=makeQuery(id+"F1.opExtrude","CAP_FACE",FACE,{"disambiguationData":[OSD([sQuery(id+"F0.wireOp",EDGE,"E0.bottom"),sQuery(id+"F0.wireOp",EDGE,"E0.top"),sQuery(id+"F0.wireOp",EDGE,"E0.left"),sQuery(id+"F0.wireOp",EDGE,"E1"),sQuery(id+"F0.wireOp",EDGE,"E2"),sQuery(id+"F0.wireOp",EDGE,"E3.1.0.0"),sQuery(id+"F0.wireOp",EDGE,"E3.1.0.1"),sQuery(id+"F0.wireOp",EDGE,"E3.2.0.0"),sQuery(id+"F0.wireOp",EDGE,"E3.2.0.1"),sQuery(id+"F0.wireOp",EDGE,"E4"),sQuery(id+"F0.wireOp",EDGE,"E5"),sQuery(id+"F0.wireOp",EDGE,"E7"),sQuery(id+"F0.wireOp",EDGE,"E8"),sQuery(id+"F0.wireOp",EDGE,"E9.trimOffspring"),sQuery(id+"F0.wireOp",EDGE,"E10.trimOffspring"),sQuery(id+"F0.wireOp",EDGE,"E11.trimOffspring"),sQuery(id+"F0.wireOp",EDGE,"E12.trimOffspring")])],"isStart":true});
            var sketch = newSketch(context, id + "F4", { "sketchPlane" : qUnion([Q0])});
            skLineSegment(sketch, "E41.bottom", {"start": v(-14400, 3200) * mm, "end": v(0, 3200) * mm});
            skLineSegment(sketch, "E41.top", {"start": v(-14400, 422) * mm, "end": v(0, 422) * mm});
            skLineSegment(sketch, "E41.left", {"start": v(-14400, 3200) * mm, "end": v(-14400, 422) * mm});
            skLineSegment(sketch, "E41.right", {"start": v(0, 3200) * mm, "end": v(0, 422) * mm});
            skLineSegment(sketch, "E42.bottom", {"start": v(0, 1350) * mm, "end": v(-1749, 1350) * mm});
            skLineSegment(sketch, "E42.top", {"start": v(0, 2550) * mm, "end": v(-1749, 2550) * mm});
            skLineSegment(sketch, "E42.left", {"start": v(0, 1350) * mm, "end": v(0, 2550) * mm});
            skLineSegment(sketch, "E42.right", {"start": v(-1749, 1350) * mm, "end": v(-1749, 2550) * mm});
            skLineSegment(sketch, "E43.bottom", {"start": v(-7200, 2000) * mm, "end": v(-8898, 2000) * mm});
            skLineSegment(sketch, "E43.top", {"start": v(-7200, 2550) * mm, "end": v(-8898, 2550) * mm});
            skLineSegment(sketch, "E43.left", {"start": v(-7200, 2550) * mm, "end": v(-7200, 2000) * mm});
            skLineSegment(sketch, "E43.right", {"start": v(-8898, 2550) * mm, "end": v(-8898, 2000) * mm});
            skLineSegment(sketch, "E44.bottom", {"start": v(-9000, 2550) * mm, "end": v(-10698, 2550) * mm});
            skLineSegment(sketch, "E44.top", {"start": v(-9000, 1350) * mm, "end": v(-10698, 1350) * mm});
            skLineSegment(sketch, "E44.left", {"start": v(-9000, 2550) * mm, "end": v(-9000, 1350) * mm});
            skLineSegment(sketch, "E44.right", {"start": v(-10698, 2550) * mm, "end": v(-10698, 1350) * mm});
            skSolve(sketch);
        }
        {
            var Q0;
            Q0=makeQuery(id+"F4.imprint","IMPRINT",FACE,{"disambiguationData":[TD([[makeQuery(id+"F4.imprint","IMPRINT",EDGE,{"derivedFrom":sQuery(id+"F4.wireOp",EDGE,"E41.bottom")}),-1.0]])]});
            var Q1;
            {var subQ4=sQuery(id+"F0.wireOp",EDGE,"E1");var subQ7=sQuery(id+"F0.wireOp",EDGE,"E0.top");var subQ8=makeQuery(id+"F1.opExtrude","CAP_EDGE",EDGE,{"disambiguationData":[OSD([subQ7]),TDD([makeQuery(id+"F0.imprint","IMPRINT",EDGE,{"disambiguationData":[TD([[makeQuery(id+"F0.imprint","INTERSECT",VERTEX,{"derivedFrom":[subQ7,subQ4]}),-1.0]])],"derivedFrom":subQ7})])],"isStart":true});Q1=makeQuery(id+"F4.imprint","IMPRINT",FACE,{"disambiguationData":[TD([[makeQuery(id+"F4.imprint","IMPRINT",EDGE,{"derivedFrom":subQ8}),1.0]])]});}
            var Q2;
            {var subQ0=sQuery(id+"F4.wireOp",EDGE,"E41.bottom");var subQ1=makeQuery(id+"F1.opExtrude","CAP_EDGE",EDGE,{"disambiguationData":[OSD([sQuery(id+"F0.wireOp",EDGE,"E1")])],"isStart":true});var subQ2=makeQuery(id+"F4.imprint","INTERSECT",VERTEX,{"derivedFrom":[subQ1,subQ0]});var subQ3=makeQuery(id+"F1.opExtrude","CAP_EDGE",EDGE,{"disambiguationData":[OSD([sQuery(id+"F0.wireOp",EDGE,"E2")])],"isStart":true});var subQ4=makeQuery(id+"F4.imprint","INTERSECT",VERTEX,{"derivedFrom":[subQ3,subQ0]});Q2=makeQuery(id+"F4.imprint","IMPRINT",FACE,{"disambiguationData":[TD([[makeQuery(id+"F4.imprint","IMPRINT",EDGE,{"disambiguationData":[TD([[subQ2,-1.0],[subQ4,1.0]])],"derivedFrom":subQ0}),1.0]])]});}
            var Q3;
            {var subQ3=sQuery(id+"F4.wireOp",EDGE,"E41.left");Q3=makeQuery(id+"F4.imprint","IMPRINT",FACE,{"disambiguationData":[TD([[makeQuery(id+"F4.imprint","IMPRINT",EDGE,{"derivedFrom":subQ3}),1.0]])]});}
            var Q4;
            {var subQ6=sQuery(id+"F0.wireOp",EDGE,"E8");var subQ7=makeQuery(id+"F1.opExtrude","CAP_EDGE",EDGE,{"disambiguationData":[OSD([subQ6]),TDD([makeQuery(id+"F0.imprint","IMPRINT",EDGE,{"disambiguationData":[TD([[makeQuery(id+"F0.imprint","INTERSECT",VERTEX,{"derivedFrom":[sQuery(id+"F0.wireOp",EDGE,"E0.left"),subQ6]}),1.0]])],"derivedFrom":subQ6})])],"isStart":true});Q4=makeQuery(id+"F4.imprint","IMPRINT",FACE,{"disambiguationData":[TD([[makeQuery(id+"F4.imprint","IMPRINT",EDGE,{"derivedFrom":subQ7}),-1.0]])]});}
            var Q5;
            {var subQ4=sQuery(id+"F0.wireOp",EDGE,"E10.trimOffspring");var subQ7=sQuery(id+"F0.wireOp",EDGE,"E8");var subQ8=makeQuery(id+"F1.opExtrude","CAP_EDGE",EDGE,{"disambiguationData":[OSD([subQ7]),TDD([makeQuery(id+"F0.imprint","IMPRINT",EDGE,{"disambiguationData":[TD([[makeQuery(id+"F0.imprint","INTERSECT",VERTEX,{"derivedFrom":[subQ7,subQ4]}),1.0]])],"derivedFrom":subQ7})])],"isStart":true});Q5=makeQuery(id+"F4.imprint","IMPRINT",FACE,{"disambiguationData":[TD([[makeQuery(id+"F4.imprint","IMPRINT",EDGE,{"derivedFrom":subQ8}),-1.0]])]});}
            var Q6;
            {var subQ1=sQuery(id+"F0.wireOp",EDGE,"E3.2.0.0");var subQ2=sQuery(id+"F0.wireOp",EDGE,"E8");var subQ3=makeQuery(id+"F0.imprint","INTERSECT",VERTEX,{"derivedFrom":[subQ1,subQ2]});var subQ9=makeQuery(id+"F1.opExtrude","CAP_EDGE",EDGE,{"disambiguationData":[OSD([subQ2]),TDD([makeQuery(id+"F0.imprint","IMPRINT",EDGE,{"disambiguationData":[TD([[subQ3,-1.0]])],"derivedFrom":subQ2})])],"isStart":true});Q6=makeQuery(id+"F4.imprint","IMPRINT",FACE,{"disambiguationData":[TD([[makeQuery(id+"F4.imprint","IMPRINT",EDGE,{"derivedFrom":subQ9}),-1.0]])]});}
            extrude(context, id + "F5", {"entities" : qUnion([Q0, Q1, Q2, Q3, Q4, Q5, Q6]), "operationType" : NewBodyOperationType.ADD, "depth" : 12 * mm, "offsetDistance" : 25 * mm});
        }
        {
            var Q0;
            Q0=makeQuery(id+"F3.opExtrude","SWEPT_FACE",FACE,{"disambiguationData":[OSD([sQuery(id+"F2.wireOp",EDGE,"E37.right")])]});
            var sketch = newSketch(context, id + "F6", { "sketchPlane" : qUnion([Q0])});
            skLineSegment(sketch, "E45", {"start": v(-400, 0) * mm, "end": v(-400, 2900) * mm});
            skLineSegment(sketch, "E46", {"start": v(-400, 2900) * mm, "end": v(12, 2995.12) * mm});
            skLineSegment(sketch, "E47", {"start": v(12, 2995.12) * mm, "end": v(12, 0) * mm});
            skLineSegment(sketch, "E48", {"start": v(12, 0) * mm, "end": v(-422, 0) * mm});
            skLineSegment(sketch, "E49", {"start": v(-422, 0) * mm, "end": v(-422, 2894.92) * mm});
            skLineSegment(sketch, "E50", {"start": v(-422, 2894.92) * mm, "end": v(-400, 2900) * mm});
            skLineSegment(sketch, "E51", {"start": v(12, 2995.12) * mm, "end": v(12, 3245.12) * mm});
            skLineSegment(sketch, "E52", {"start": v(12, 3245.12) * mm, "end": v(-422, 3245.12) * mm});
            skLineSegment(sketch, "E53", {"start": v(-422, 3245.12) * mm, "end": v(-422, 2894.92) * mm});
            skLineSegment(sketch, "E54", {"start": v(-422, 2894.92) * mm, "end": v(-452, 2888) * mm});
            skLineSegment(sketch, "E55", {"start": v(-452, 2888) * mm, "end": v(-452, 3245.12) * mm});
            skLineSegment(sketch, "E56", {"start": v(-452, 3245.12) * mm, "end": v(-422, 3245.12) * mm});
            skSolve(sketch);
        }
        {
            var Q0;
            Q0=makeQuery(id+"F6.imprint","IMPRINT",FACE,{"disambiguationData":[TD([[makeQuery(id+"F6.imprint","IMPRINT",EDGE,{"derivedFrom":sQuery(id+"F6.wireOp",EDGE,"E53")}),-1.0]])]});
            var Q1;
            {var subQ1=sQuery(id+"F2.wireOp",EDGE,"E37.right");var subQ6=makeQuery(id+"F3.opExtrude","SWEPT_EDGE",EDGE,{"disambiguationData":[OSD([sQuery(id+"F2.wireOp",EDGE,"E37.bottom"),subQ1])]});Q1=makeQuery(id+"F6.imprint","IMPRINT",FACE,{"disambiguationData":[TD([[makeQuery(id+"F6.imprint","IMPRINT",EDGE,{"derivedFrom":subQ6}),-1.0]])]});}
            var Q2;
            {var subQ5=sQuery(id+"F6.wireOp",EDGE,"E46");Q2=makeQuery(id+"F6.imprint","IMPRINT",FACE,{"disambiguationData":[TD([[makeQuery(id+"F6.imprint","IMPRINT",EDGE,{"derivedFrom":subQ5}),1.0]])]});}
            extrude(context, id + "F7", {"entities" : qUnion([Q0, Q1, Q2]), "operationType" : NewBodyOperationType.REMOVE, "endBound" : BoundingType.THROUGH_ALL, "oppositeDirection" : true, "depth" : 25 * mm, "offsetDistance" : 25 * mm});
        }
        {
            var Q0;
            {var subQ0=sQuery(id+"F0.wireOp",EDGE,"E0.bottom");Q0=makeQuery(id+"F3.boolean.opBoolean","MERGE",FACE,{"derivedFrom":[makeQuery(id+"F1.opExtrude","SWEPT_FACE",FACE,{"disambiguationData":[OSD([subQ0]),TDD([makeQuery(id+"F0.imprint","IMPRINT",EDGE,{"disambiguationData":[TD([[makeQuery(id+"F0.imprint","INTERSECT",VERTEX,{"derivedFrom":[subQ0,sQuery(id+"F0.wireOp",EDGE,"E1")]}),-1.0]])],"derivedFrom":subQ0})])]}),makeQuery(id+"F1.opExtrude","SWEPT_FACE",FACE,{"disambiguationData":[OSD([subQ0]),TDD([makeQuery(id+"F0.imprint","IMPRINT",EDGE,{"disambiguationData":[TD([[makeQuery(id+"F0.imprint","INTERSECT",VERTEX,{"derivedFrom":[subQ0,sQuery(id+"F0.wireOp",EDGE,"E3.1.0.0")]}),-1.0]])],"derivedFrom":subQ0})])]}),makeQuery(id+"F1.opExtrude","SWEPT_FACE",FACE,{"disambiguationData":[OSD([subQ0]),TDD([makeQuery(id+"F0.imprint","IMPRINT",EDGE,{"disambiguationData":[TD([[makeQuery(id+"F0.imprint","INTERSECT",VERTEX,{"derivedFrom":[subQ0,sQuery(id+"F0.wireOp",EDGE,"E3.2.0.0")]}),-1.0]])],"derivedFrom":subQ0})])]}),makeQuery(id+"F1.opExtrude","SWEPT_FACE",FACE,{"disambiguationData":[OSD([subQ0]),TDD([makeQuery(id+"F0.imprint","IMPRINT",EDGE,{"disambiguationData":[TD([[makeQuery(id+"F0.imprint","INTERSECT",VERTEX,{"derivedFrom":[subQ0,sQuery(id+"F0.wireOp",EDGE,"E3.3.0.0")]}),-1.0]])],"derivedFrom":subQ0})])]}),makeQuery(id+"F1.opExtrude","SWEPT_FACE",FACE,{"disambiguationData":[OSD([subQ0]),TDD([makeQuery(id+"F0.imprint","IMPRINT",EDGE,{"disambiguationData":[TD([[makeQuery(id+"F0.imprint","INTERSECT",VERTEX,{"derivedFrom":[subQ0,sQuery(id+"F0.wireOp",EDGE,"E3.4.0.0")]}),-1.0]])],"derivedFrom":subQ0})])]}),makeQuery(id+"F1.opExtrude","SWEPT_FACE",FACE,{"disambiguationData":[OSD([subQ0]),TDD([makeQuery(id+"F0.imprint","IMPRINT",EDGE,{"disambiguationData":[TD([[makeQuery(id+"F0.imprint","INTERSECT",VERTEX,{"derivedFrom":[subQ0,sQuery(id+"F0.wireOp",EDGE,"E3.5.0.0")]}),-1.0]])],"derivedFrom":subQ0})])]}),makeQuery(id+"F1.opExtrude","SWEPT_FACE",FACE,{"disambiguationData":[OSD([subQ0]),TDD([makeQuery(id+"F0.imprint","IMPRINT",EDGE,{"disambiguationData":[TD([[makeQuery(id+"F0.imprint","INTERSECT",VERTEX,{"derivedFrom":[subQ0,sQuery(id+"F0.wireOp",EDGE,"E3.6.0.0")]}),-1.0]])],"derivedFrom":subQ0})])]}),makeQuery(id+"F1.opExtrude","SWEPT_FACE",FACE,{"disambiguationData":[OSD([subQ0]),TDD([makeQuery(id+"F0.imprint","IMPRINT",EDGE,{"disambiguationData":[TD([[makeQuery(id+"F0.imprint","INTERSECT",VERTEX,{"derivedFrom":[subQ0,sQuery(id+"F0.wireOp",EDGE,"E3.7.0.0")]}),-1.0]])],"derivedFrom":subQ0})])]}),makeQuery(id+"F1.opExtrude","SWEPT_FACE",FACE,{"disambiguationData":[OSD([subQ0]),TDD([makeQuery(id+"F0.imprint","IMPRINT",EDGE,{"disambiguationData":[TD([[makeQuery(id+"F0.imprint","INTERSECT",VERTEX,{"derivedFrom":[subQ0,sQuery(id+"F0.wireOp",EDGE,"E3.8.0.0")]}),-1.0]])],"derivedFrom":subQ0})])]}),makeQuery(id+"F1.opExtrude","SWEPT_FACE",FACE,{"disambiguationData":[OSD([subQ0]),TDD([makeQuery(id+"F0.imprint","IMPRINT",EDGE,{"disambiguationData":[TD([[makeQuery(id+"F0.imprint","INTERSECT",VERTEX,{"derivedFrom":[subQ0,sQuery(id+"F0.wireOp",EDGE,"E3.9.0.0")]}),-1.0]])],"derivedFrom":subQ0})])]}),makeQuery(id+"F1.opExtrude","SWEPT_FACE",FACE,{"disambiguationData":[OSD([subQ0]),TDD([makeQuery(id+"F0.imprint","IMPRINT",EDGE,{"disambiguationData":[TD([[makeQuery(id+"F0.imprint","INTERSECT",VERTEX,{"derivedFrom":[subQ0,sQuery(id+"F0.wireOp",EDGE,"E3.10.0.0")]}),-1.0]])],"derivedFrom":subQ0})])]}),makeQuery(id+"F1.opExtrude","SWEPT_FACE",FACE,{"disambiguationData":[OSD([subQ0]),TDD([makeQuery(id+"F0.imprint","IMPRINT",EDGE,{"disambiguationData":[TD([[makeQuery(id+"F0.imprint","INTERSECT",VERTEX,{"derivedFrom":[subQ0,sQuery(id+"F0.wireOp",EDGE,"E3.11.0.0")]}),-1.0]])],"derivedFrom":subQ0})])]}),makeQuery(id+"F1.opExtrude","SWEPT_FACE",FACE,{"disambiguationData":[OSD([subQ0]),TDD([makeQuery(id+"F0.imprint","IMPRINT",EDGE,{"disambiguationData":[TD([[makeQuery(id+"F0.imprint","INTERSECT",VERTEX,{"derivedFrom":[subQ0,sQuery(id+"F0.wireOp",EDGE,"E3.12.0.0")]}),-1.0]])],"derivedFrom":subQ0})])]}),makeQuery(id+"F1.opExtrude","SWEPT_FACE",FACE,{"disambiguationData":[OSD([subQ0]),TDD([makeQuery(id+"F0.imprint","IMPRINT",EDGE,{"disambiguationData":[TD([[makeQuery(id+"F0.imprint","INTERSECT",VERTEX,{"derivedFrom":[subQ0,sQuery(id+"F0.wireOp",EDGE,"E3.13.0.0")]}),-1.0]])],"derivedFrom":subQ0})])]}),makeQuery(id+"F1.opExtrude","SWEPT_FACE",FACE,{"disambiguationData":[OSD([subQ0]),TDD([makeQuery(id+"F0.imprint","IMPRINT",EDGE,{"disambiguationData":[TD([[makeQuery(id+"F0.imprint","INTERSECT",VERTEX,{"derivedFrom":[subQ0,sQuery(id+"F0.wireOp",EDGE,"E3.14.0.0")]}),-1.0]])],"derivedFrom":subQ0})])]}),makeQuery(id+"F1.opExtrude","SWEPT_FACE",FACE,{"disambiguationData":[OSD([subQ0]),TDD([makeQuery(id+"F0.imprint","IMPRINT",EDGE,{"disambiguationData":[TD([[makeQuery(id+"F0.imprint","INTERSECT",VERTEX,{"derivedFrom":[subQ0,sQuery(id+"F0.wireOp",EDGE,"E3.15.0.0")]}),-1.0]])],"derivedFrom":subQ0})])]}),makeQuery(id+"F1.opExtrude","SWEPT_FACE",FACE,{"disambiguationData":[OSD([subQ0]),TDD([makeQuery(id+"F0.imprint","IMPRINT",EDGE,{"disambiguationData":[TD([[makeQuery(id+"F0.imprint","INTERSECT",VERTEX,{"derivedFrom":[subQ0,sQuery(id+"F0.wireOp",EDGE,"E3.16.0.0")]}),-1.0]])],"derivedFrom":subQ0})])]}),makeQuery(id+"F1.opExtrude","SWEPT_FACE",FACE,{"disambiguationData":[OSD([subQ0]),TDD([makeQuery(id+"F0.imprint","IMPRINT",EDGE,{"disambiguationData":[TD([[makeQuery(id+"F0.imprint","INTERSECT",VERTEX,{"derivedFrom":[subQ0,sQuery(id+"F0.wireOp",EDGE,"E3.17.0.0")]}),-1.0]])],"derivedFrom":subQ0})])]}),makeQuery(id+"F1.opExtrude","SWEPT_FACE",FACE,{"disambiguationData":[OSD([subQ0]),TDD([makeQuery(id+"F0.imprint","IMPRINT",EDGE,{"disambiguationData":[TD([[makeQuery(id+"F0.imprint","INTERSECT",VERTEX,{"derivedFrom":[subQ0,sQuery(id+"F0.wireOp",EDGE,"E3.18.0.0")]}),-1.0]])],"derivedFrom":subQ0})])]}),makeQuery(id+"F1.opExtrude","SWEPT_FACE",FACE,{"disambiguationData":[OSD([subQ0]),TDD([makeQuery(id+"F0.imprint","IMPRINT",EDGE,{"disambiguationData":[TD([[makeQuery(id+"F0.imprint","INTERSECT",VERTEX,{"derivedFrom":[subQ0,sQuery(id+"F0.wireOp",EDGE,"E3.19.0.0")]}),-1.0]])],"derivedFrom":subQ0})])]}),makeQuery(id+"F1.opExtrude","SWEPT_FACE",FACE,{"disambiguationData":[OSD([subQ0]),TDD([makeQuery(id+"F0.imprint","IMPRINT",EDGE,{"disambiguationData":[TD([[makeQuery(id+"F0.imprint","INTERSECT",VERTEX,{"derivedFrom":[subQ0,sQuery(id+"F0.wireOp",EDGE,"E3.20.0.0")]}),-1.0]])],"derivedFrom":subQ0})])]}),makeQuery(id+"F1.opExtrude","SWEPT_FACE",FACE,{"disambiguationData":[OSD([subQ0]),TDD([makeQuery(id+"F0.imprint","IMPRINT",EDGE,{"disambiguationData":[TD([[makeQuery(id+"F0.imprint","INTERSECT",VERTEX,{"derivedFrom":[subQ0,sQuery(id+"F0.wireOp",EDGE,"E3.21.0.0")]}),-1.0]])],"derivedFrom":subQ0})])]}),makeQuery(id+"F1.opExtrude","SWEPT_FACE",FACE,{"disambiguationData":[OSD([subQ0]),TDD([makeQuery(id+"F0.imprint","IMPRINT",EDGE,{"disambiguationData":[TD([[makeQuery(id+"F0.imprint","INTERSECT",VERTEX,{"derivedFrom":[subQ0,sQuery(id+"F0.wireOp",EDGE,"E3.22.0.0")]}),-1.0]])],"derivedFrom":subQ0})])]}),makeQuery(id+"F3.opExtrude","SWEPT_FACE",FACE,{"disambiguationData":[OSD([sQuery(id+"F2.wireOp",EDGE,"E37.top")])]})]});}
            var sketch = newSketch(context, id + "F8", { "sketchPlane" : qUnion([Q0])});
            skLineSegment(sketch, "E57.bottom", {"start": v(412, -14400) * mm, "end": v(0, -14400) * mm});
            skLineSegment(sketch, "E57.top", {"start": v(412, 0) * mm, "end": v(0, 0) * mm});
            skLineSegment(sketch, "E57.left", {"start": v(412, -14400) * mm, "end": v(412, 0) * mm});
            skLineSegment(sketch, "E57.right", {"start": v(0, -14400) * mm, "end": v(0, 0) * mm});
            skSolve(sketch);
        }
        {
            var Q0;
            Q0 = qSketchRegion(id + "F8", true);
            extrude(context, id + "F9", {"entities" : qUnion([Q0]), "operationType" : NewBodyOperationType.ADD, "depth" : 12 * mm});
        }
    });
